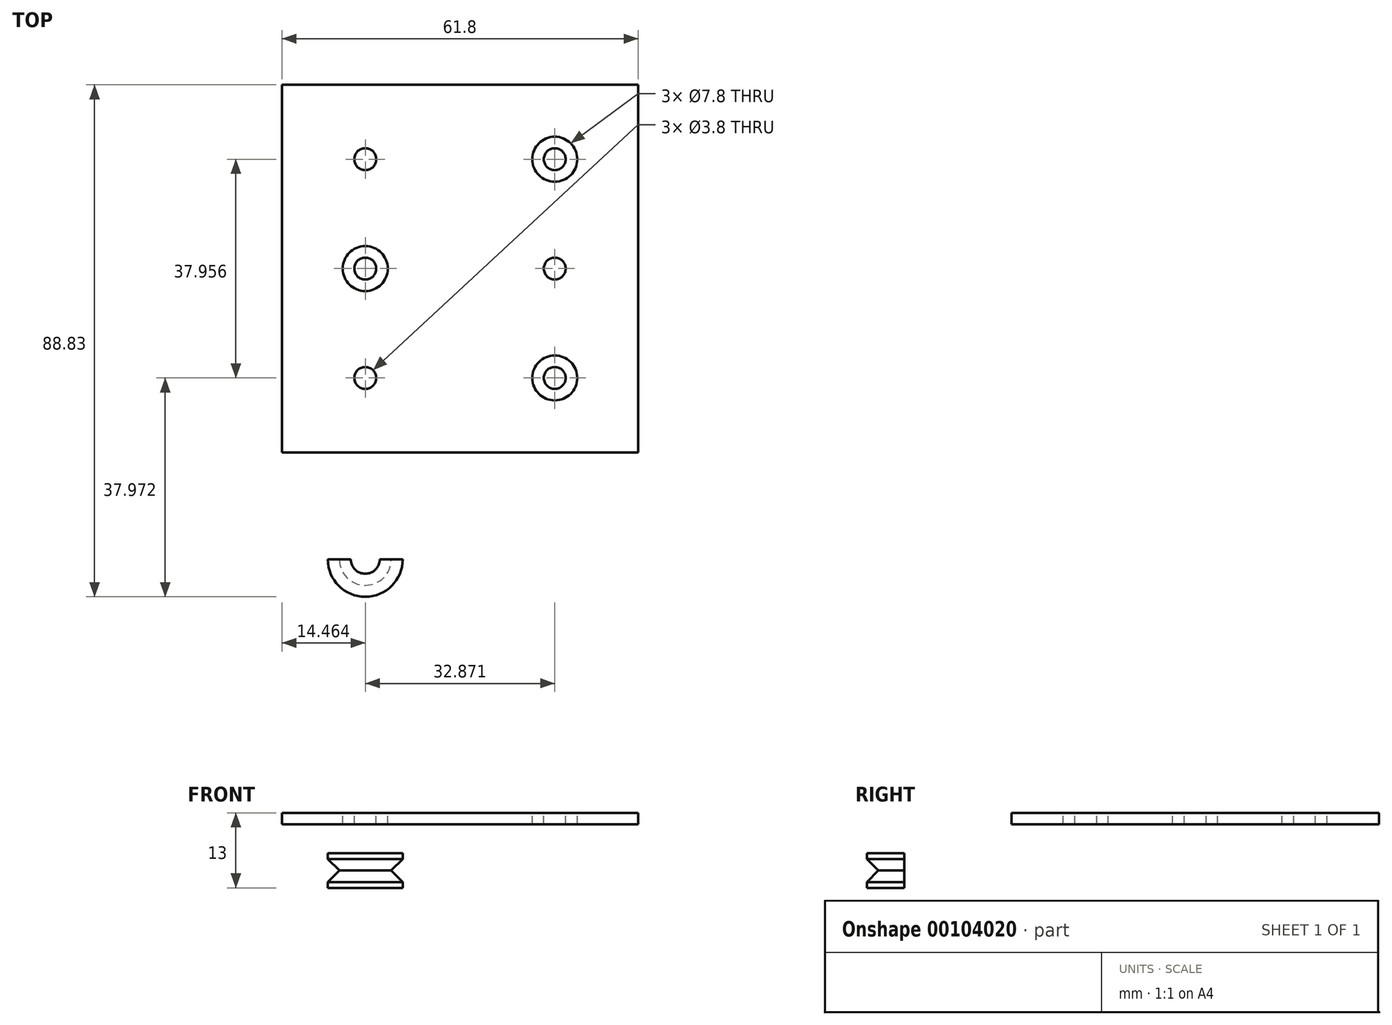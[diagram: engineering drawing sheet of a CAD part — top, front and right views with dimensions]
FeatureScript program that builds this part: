
annotation { "Feature Type Name" : "Feature", "Feature Type Description" : "" }
export const myFeature = defineFeature(function(context is Context, id is Id, definition is map)
    precondition{}
    {
        {
            var Q0;
            Q0=qCreatedBy(makeId("Top.planeOp"),FACE);
            var sketch = newSketch(context, id + "F0", { "sketchPlane" : qUnion([Q0])});
            skLineSegment(sketch, "E0.bottom", {"start": v(-30.9, 50.45) * mm, "end": v(30.9, 50.45) * mm});
            skLineSegment(sketch, "E0.top", {"start": v(-30.9, -50.45) * mm, "end": v(30.9, -50.45) * mm});
            skLineSegment(sketch, "E0.left", {"start": v(-30.9, 50.45) * mm, "end": v(-30.9, -50.45) * mm});
            skLineSegment(sketch, "E0.right", {"start": v(30.9, 50.45) * mm, "end": v(30.9, -50.45) * mm});
            skPoint(sketch, "E0.middle", {"position": v(0, 0) * mm});
            skSolve(sketch);
        }
        {
            var Q0;
            Q0=makeQuery(id+"F0.imprint","IMPRINT",FACE,{"disambiguationData":[TD([[makeQuery(id+"F0.imprint","IMPRINT",EDGE,{"derivedFrom":sQuery(id+"F0.wireOp",EDGE,"E0.bottom")}),-1.0]])]});
            extrude(context, id + "F1", {"entities" : qUnion([Q0]), "depth" : 5 * mm});
        }
        {
            var Q0;
            Q0=makeQuery(id+"F1.opExtrude","SWEPT_FACE",FACE,{"disambiguationData":[OSD([sQuery(id+"F0.wireOp",EDGE,"E0.top")])]});
            var sketch = newSketch(context, id + "F2", { "sketchPlane" : qUnion([Q0])});
            skLineSegment(sketch, "E1", {"start": v(0, 0) * mm, "end": v(0, 5) * mm, "construction": true});
            skCircle(sketch, "E2", {"center": v(-8.4, -5) * mm, "radius": 2.5 * mm, "construction": true});
            skCircle(sketch, "E3.MirrorC", {"center": v(8.4, -5) * mm, "radius": 2.5 * mm, "construction": true});
            skLineSegment(sketch, "E4.bottom", {"start": v(-13.94, -2) * mm, "end": v(-9.94, -2) * mm});
            skLineSegment(sketch, "E4.top", {"start": v(-13.94, -8) * mm, "end": v(-9.94, -8) * mm});
            skLineSegment(sketch, "E4.left", {"start": v(-13.94, -2) * mm, "end": v(-13.94, -8) * mm});
            skLineSegment(sketch, "E4.right", {"start": v(-9.94, -2) * mm, "end": v(-9.94, -8) * mm});
            skPoint(sketch, "E4.middle", {"position": v(-11.94, -5) * mm});
            skLineSegment(sketch, "E5", {"start": v(-16.44, -2) * mm, "end": v(-16.44, -8) * mm});
            skLineSegment(sketch, "E6", {"start": v(-11.94, -5) * mm, "end": v(-9.94, -3) * mm});
            skLineSegment(sketch, "E7", {"start": v(-11.94, -5) * mm, "end": v(-9.94, -5) * mm, "construction": true});
            skLineSegment(sketch, "E8.MirrorCS", {"start": v(-11.94, -5) * mm, "end": v(-9.94, -7) * mm});
            skSolve(sketch);
        }
        {
            var Q0;
            {var subQ1=sQuery(id+"F2.wireOp",EDGE,"E4.bottom");Q0=makeQuery(id+"F2.imprint","IMPRINT",FACE,{"disambiguationData":[TD([[makeQuery(id+"F2.imprint","IMPRINT",EDGE,{"derivedFrom":subQ1}),-1.0]])]});}
            var Q1;
            Q1=sQuery(id+"F2.wireOp",EDGE,"E5");
            revolve(context, id + "F3", {"entities" : qUnion([Q0]), "axis" : qUnion([Q1]), "revolveType" : RevolveType.FULL});
        }
        {
            var Q0;
            Q0=makeQuery(id+"F1.opExtrude","CAP_FACE",FACE,{"disambiguationData":[OSD([sQuery(id+"F0.wireOp",EDGE,"E0.bottom"),sQuery(id+"F0.wireOp",EDGE,"E0.top"),sQuery(id+"F0.wireOp",EDGE,"E0.left"),sQuery(id+"F0.wireOp",EDGE,"E0.right")])],"isStart":false});
            var sketch = newSketch(context, id + "F4", { "sketchPlane" : qUnion([Q0])});
            skPoint(sketch, "E9.0", {"position": v(-16.44, -50.45) * mm});
            skLineSegment(sketch, "E10", {"start": v(0, -50.45) * mm, "end": v(0, 50.45) * mm, "construction": true});
            skCircle(sketch, "E11", {"center": v(-16.44, -18.98) * mm, "radius": 1.9 * mm});
            skCircle(sketch, "E12.1.0", {"center": v(16.44, 0) * mm, "radius": 1.9 * mm});
            skCircle(sketch, "E12.2.0", {"center": v(-16.44, 18.98) * mm, "radius": 1.9 * mm});
            skPoint(sketch, "E12.center", {"position": v(-5.48, 0) * mm});
            skPoint(sketch, "E13.MirrorP", {"position": v(5.48, 0) * mm});
            skCircle(sketch, "E14.MirrorC", {"center": v(16.44, -18.98) * mm, "radius": 1.9 * mm});
            skCircle(sketch, "E15.MirrorC", {"center": v(-16.44, 0) * mm, "radius": 1.9 * mm});
            skCircle(sketch, "E16.MirrorC", {"center": v(16.44, 18.98) * mm, "radius": 1.9 * mm});
            skCircle(sketch, "E17.0", {"center": v(-16.44, 18.98) * mm, "radius": 3.9 * mm});
            skCircle(sketch, "E18.0", {"center": v(-16.44, -18.98) * mm, "radius": 3.9 * mm});
            skCircle(sketch, "E19.0", {"center": v(-16.44, 0) * mm, "radius": 3.9 * mm});
            skCircle(sketch, "E20.MirrorC", {"center": v(16.44, 18.98) * mm, "radius": 3.9 * mm});
            skCircle(sketch, "E21.MirrorC", {"center": v(16.44, 0) * mm, "radius": 3.9 * mm});
            skCircle(sketch, "E22.MirrorC", {"center": v(16.44, -18.98) * mm, "radius": 3.9 * mm});
            skLineSegment(sketch, "E23.bottom", {"start": v(-30.9, -31.88) * mm, "end": v(30.9, -31.88) * mm});
            skLineSegment(sketch, "E23.top", {"start": v(-30.9, 31.88) * mm, "end": v(30.9, 31.88) * mm});
            skLineSegment(sketch, "E23.left", {"start": v(-30.9, -31.88) * mm, "end": v(-30.9, 31.88) * mm});
            skLineSegment(sketch, "E23.right", {"start": v(30.9, -31.88) * mm, "end": v(30.9, 31.88) * mm});
            skPoint(sketch, "E23.middle", {"position": v(0, 0) * mm});
            skSolve(sketch);
        }
        {
            var Q0;
            Q0=makeQuery(id+"F4.imprint","IMPRINT",FACE,{"disambiguationData":[TD([[makeQuery(id+"F4.imprint","IMPRINT",EDGE,{"derivedFrom":sQuery(id+"F4.wireOp",EDGE,"E15.MirrorC")}),-1.0]])]});
            var Q1;
            Q1=makeQuery(id+"F4.imprint","IMPRINT",FACE,{"disambiguationData":[TD([[makeQuery(id+"F4.imprint","IMPRINT",EDGE,{"derivedFrom":sQuery(id+"F4.wireOp",EDGE,"E11")}),1.0]])]});
            var Q2;
            Q2=makeQuery(id+"F4.imprint","IMPRINT",FACE,{"disambiguationData":[TD([[makeQuery(id+"F4.imprint","IMPRINT",EDGE,{"derivedFrom":sQuery(id+"F4.wireOp",EDGE,"E16.MirrorC")}),-1.0]])]});
            var Q3;
            Q3=makeQuery(id+"F4.imprint","IMPRINT",FACE,{"disambiguationData":[TD([[makeQuery(id+"F4.imprint","IMPRINT",EDGE,{"derivedFrom":sQuery(id+"F4.wireOp",EDGE,"E12.1.0")}),1.0]])]});
            var Q4;
            Q4=makeQuery(id+"F4.imprint","IMPRINT",FACE,{"disambiguationData":[TD([[makeQuery(id+"F4.imprint","IMPRINT",EDGE,{"derivedFrom":sQuery(id+"F4.wireOp",EDGE,"E14.MirrorC")}),-1.0]])]});
            var Q5;
            Q5=makeQuery(id+"F4.imprint","IMPRINT",FACE,{"disambiguationData":[TD([[makeQuery(id+"F4.imprint","IMPRINT",EDGE,{"derivedFrom":sQuery(id+"F4.wireOp",EDGE,"E12.2.0")}),1.0]])]});
            var Q6;
            {var subQ0=sQuery(id+"F4.wireOp",EDGE,"E23.top");Q6=makeQuery(id+"F4.imprint","IMPRINT",FACE,{"disambiguationData":[TD([[makeQuery(id+"F4.imprint","IMPRINT",EDGE,{"derivedFrom":subQ0}),1.0]])]});}
            var Q7;
            {var subQ0=sQuery(id+"F4.wireOp",EDGE,"E23.bottom");Q7=makeQuery(id+"F4.imprint","IMPRINT",FACE,{"disambiguationData":[TD([[makeQuery(id+"F4.imprint","IMPRINT",EDGE,{"derivedFrom":subQ0}),-1.0]])]});}
            extrude(context, id + "F5", {"entities" : qUnion([Q0, Q1, Q2, Q3, Q4, Q5, Q6, Q7]), "operationType" : NewBodyOperationType.REMOVE, "oppositeDirection" : true, "depth" : 25 * mm});
        }
        {
            var Q0;
            Q0=makeQuery(id+"F5.boolean.opBoolean","COPY",FACE,{"derivedFrom":makeQuery(id+"F5.opExtrude","SWEPT_FACE",FACE,{"disambiguationData":[OSD([sQuery(id+"F4.wireOp",EDGE,"E23.bottom")])]})});
            var sketch = newSketch(context, id + "F6", { "sketchPlane" : qUnion([Q0])});
            skLineSegment(sketch, "E24", {"start": v(0, 0) * mm, "end": v(0, -7.73) * mm});
            skPoint(sketch, "E24.endSnap0", {"position": v(0, 0) * mm});
            skLineSegment(sketch, "E25.bottom", {"start": v(-30.9, 5) * mm, "end": v(-28.1, 5) * mm});
            skLineSegment(sketch, "E25.top", {"start": v(-30.9, 13) * mm, "end": v(-28.1, 13) * mm});
            skLineSegment(sketch, "E25.left", {"start": v(-30.9, 5) * mm, "end": v(-30.9, 13) * mm});
            skLineSegment(sketch, "E25.right", {"start": v(-28.1, 5) * mm, "end": v(-28.1, 13) * mm});
            skLineSegment(sketch, "E26.MirrorCS", {"start": v(28.1, 5) * mm, "end": v(28.1, 13) * mm});
            skLineSegment(sketch, "E27.MirrorCS", {"start": v(30.9, 13) * mm, "end": v(28.1, 13) * mm});
            skLineSegment(sketch, "E28.MirrorCS", {"start": v(30.9, 5) * mm, "end": v(30.9, 13) * mm});
            skSolve(sketch);
        }
        {
            var Q0;
            Q0=makeQuery(id+"F1.opExtrude","CAP_FACE",FACE,{"disambiguationData":[OSD([sQuery(id+"F0.wireOp",EDGE,"E0.bottom"),sQuery(id+"F0.wireOp",EDGE,"E0.top"),sQuery(id+"F0.wireOp",EDGE,"E0.left"),sQuery(id+"F0.wireOp",EDGE,"E0.right")])],"isStart":true});
            extrude(context, id + "F7", {"entities" : qUnion([Q0]), "operationType" : NewBodyOperationType.REMOVE, "oppositeDirection" : true, "depth" : 3 * mm});
        }
    });
